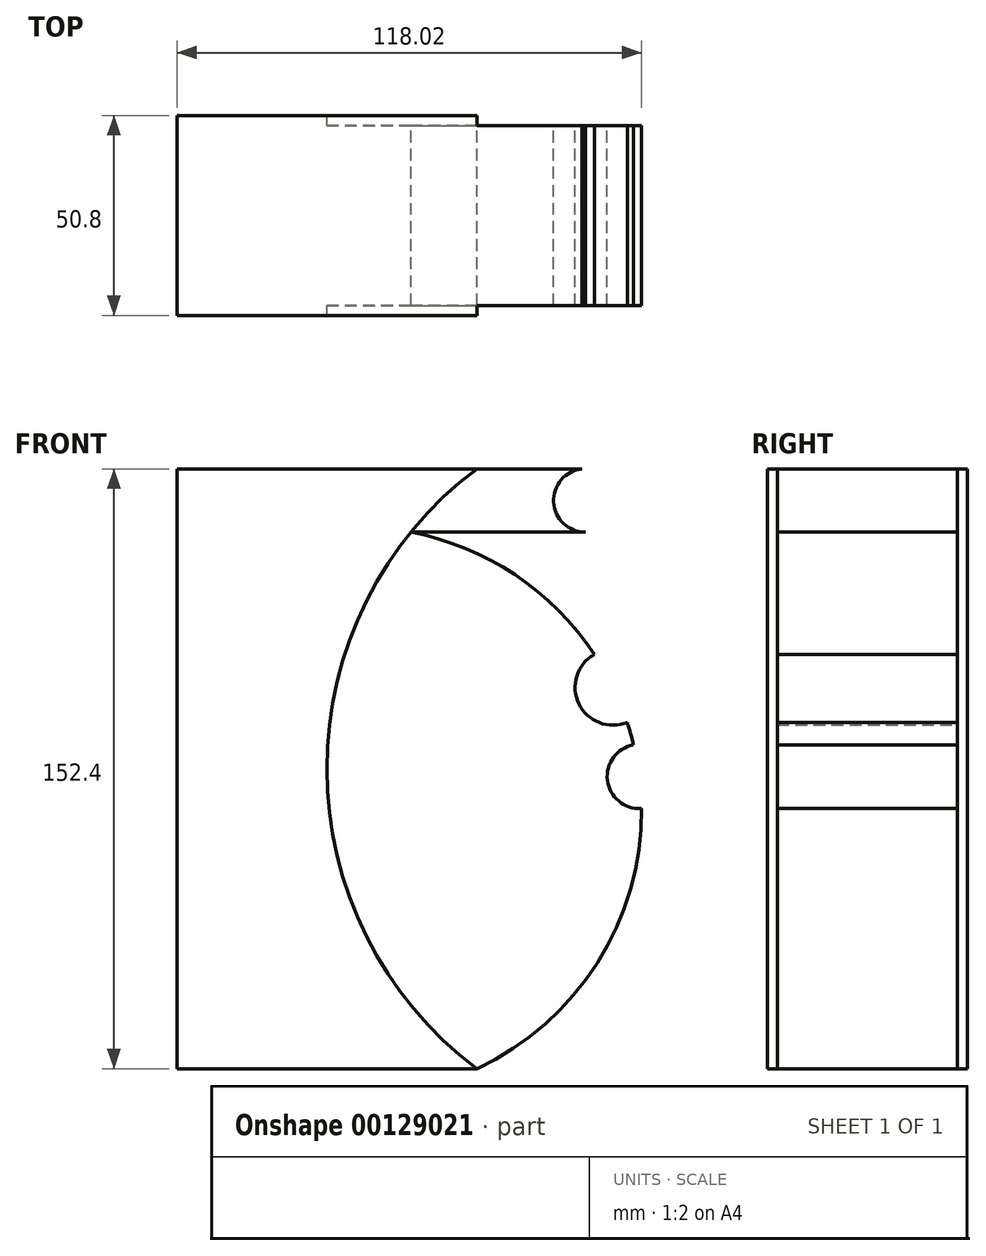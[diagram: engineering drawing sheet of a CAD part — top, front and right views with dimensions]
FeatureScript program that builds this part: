
annotation { "Feature Type Name" : "Feature", "Feature Type Description" : "" }
export const myFeature = defineFeature(function(context is Context, id is Id, definition is map)
    precondition{}
    {
        {
            var Q0;
            Q0=qCreatedBy(makeId("Front.planeOp"),FACE);
            var sketch = newSketch(context, id + "F0", { "sketchPlane" : qUnion([Q0])});
            skLineSegment(sketch, "E0.bottom", {"start": v(38.1, -76.2) * mm, "end": v(-38.1, -76.2) * mm});
            skLineSegment(sketch, "E0.top", {"start": v(38.1, 76.2) * mm, "end": v(-38.1, 76.2) * mm});
            skLineSegment(sketch, "E0.right", {"start": v(-38.1, -76.2) * mm, "end": v(-38.1, 76.2) * mm});
            skPoint(sketch, "E0.middle", {"position": v(0, 0) * mm});
            skArc(sketch, "E1", {"start": v(38.1, 76.2) * mm, "mid": v(0, 0) * mm, "end": v(38.1, -76.2) * mm});
            skLineSegment(sketch, "E2.bottom", {"start": v(17.52, 76.2) * mm, "end": v(66.57, 76.2) * mm});
            skLineSegment(sketch, "E2.top", {"start": v(20.04, 60.12) * mm, "end": v(65.7, 60.12) * mm});
            skArc(sketch, "E3", {"start": v(38.1, -76.2) * mm, "mid": v(79.38, -1.95) * mm, "end": v(21.37, 60.12) * mm});
            skArc(sketch, "E4", {"start": v(66.57, 76.2) * mm, "mid": v(57.64, 68.62) * mm, "end": v(65.7, 60.12) * mm});
            skArc(sketch, "E5", {"start": v(67.94, 29.07) * mm, "mid": v(64.04, 16.5) * mm, "end": v(76.31, 11.78) * mm});
            skArc(sketch, "E6", {"start": v(77.93, 6.09) * mm, "mid": v(71.28, -2.94) * mm, "end": v(79.91, -10.1) * mm});
            skSolve(sketch);
        }
        {
            var Q0;
            {var subQ6=sQuery(id+"F0.wireOp",EDGE,"E0.bottom");Q0=makeQuery(id+"F0.imprint","IMPRINT",FACE,{"disambiguationData":[TD([[makeQuery(id+"F0.imprint","IMPRINT",EDGE,{"derivedFrom":subQ6}),-1.0]])]});}
            extrude(context, id + "F1", {"entities" : qUnion([Q0]), "endBound" : BoundingType.SYMMETRIC, "depth" : 50.8 * mm});
        }
        {
            var Q0;
            {var subQ0=sQuery(id+"F0.wireOp",EDGE,"E4");var subQ1=sQuery(id+"F0.wireOp",EDGE,"E2.bottom");var subQ2=makeQuery(id+"F0.imprint","INTERSECT",VERTEX,{"disambiguationData":[OD(0.0)],"derivedFrom":[subQ1,subQ0]});Q0=makeQuery(id+"F0.imprint","IMPRINT",FACE,{"disambiguationData":[TD([[makeQuery(id+"F0.imprint","IMPRINT",EDGE,{"disambiguationData":[TD([[subQ2,1.0]])],"derivedFrom":subQ1}),1.0]])]});}
            var Q1;
            {var subQ0=sQuery(id+"F0.wireOp",EDGE,"E2.bottom");var subQ1=sQuery(id+"F0.wireOp",EDGE,"E1");var subQ2=makeQuery(id+"F0.imprint","INTERSECT",VERTEX,{"derivedFrom":[subQ1,subQ0]});Q1=makeQuery(id+"F0.imprint","IMPRINT",FACE,{"disambiguationData":[TD([[makeQuery(id+"F0.imprint","IMPRINT",EDGE,{"disambiguationData":[TD([[subQ2,-1.0]])],"derivedFrom":subQ0}),-1.0]])]});}
            var Q2;
            {var subQ0=sQuery(id+"F0.wireOp",EDGE,"E3");Q2=makeQuery(id+"F0.imprint","IMPRINT",FACE,{"disambiguationData":[TD([[makeQuery(id+"F0.imprint","IMPRINT",EDGE,{"derivedFrom":subQ0}),1.0]])]});}
            extrude(context, id + "F2", {"entities" : qUnion([Q0, Q1, Q2]), "operationType" : NewBodyOperationType.ADD, "endBound" : BoundingType.SYMMETRIC, "depth" : 45.72 * mm});
        }
    });
